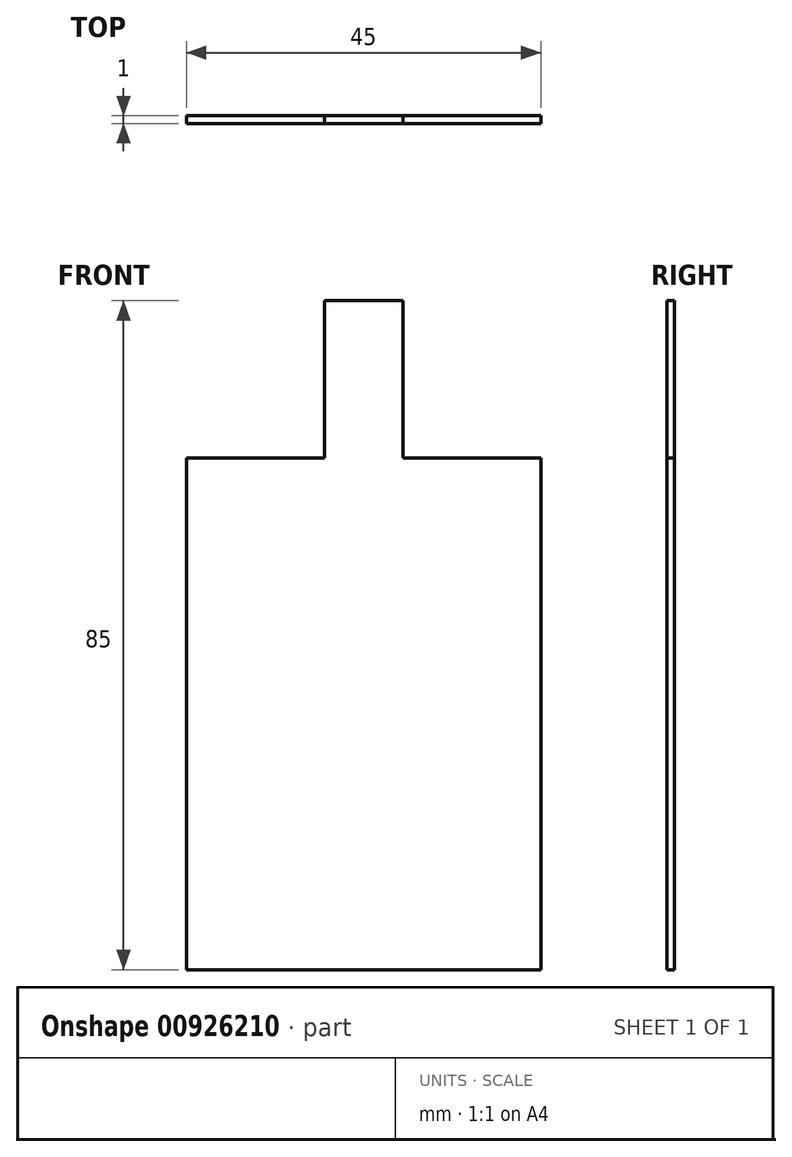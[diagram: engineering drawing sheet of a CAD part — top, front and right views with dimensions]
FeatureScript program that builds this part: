
annotation { "Feature Type Name" : "Feature", "Feature Type Description" : "" }
export const myFeature = defineFeature(function(context is Context, id is Id, definition is map)
    precondition{}
    {
        {
            var Q0;
            Q0=qCreatedBy(makeId("Front.planeOp"),FACE);
            var sketch = newSketch(context, id + "F0", { "sketchPlane" : qUnion([Q0])});
            skLineSegment(sketch, "E0.bottom", {"start": v(22.5, -32.5) * mm, "end": v(-22.5, -32.5) * mm});
            skLineSegment(sketch, "E0.top", {"start": v(22.5, 32.5) * mm, "end": v(-22.5, 32.5) * mm});
            skLineSegment(sketch, "E0.left", {"start": v(22.5, -32.5) * mm, "end": v(22.5, 32.5) * mm});
            skLineSegment(sketch, "E0.right", {"start": v(-22.5, -32.5) * mm, "end": v(-22.5, 32.5) * mm});
            skPoint(sketch, "E0.middle", {"position": v(0, 0) * mm});
            skLineSegment(sketch, "E1.bottom", {"start": v(-5, 32.5) * mm, "end": v(5, 32.5) * mm});
            skLineSegment(sketch, "E1.top", {"start": v(-5, 52.5) * mm, "end": v(5, 52.5) * mm});
            skLineSegment(sketch, "E1.left", {"start": v(-5, 32.5) * mm, "end": v(-5, 52.5) * mm});
            skLineSegment(sketch, "E1.right", {"start": v(5, 32.5) * mm, "end": v(5, 52.5) * mm});
            skSolve(sketch);
        }
        {
            var Q0;
            Q0 = qSketchRegion(id + "F0", true);
            extrude(context, id + "F1", {"entities" : qUnion([Q0]), "depth" : 1 * mm, "offsetDistance" : 25.4 * mm});
        }
    });
